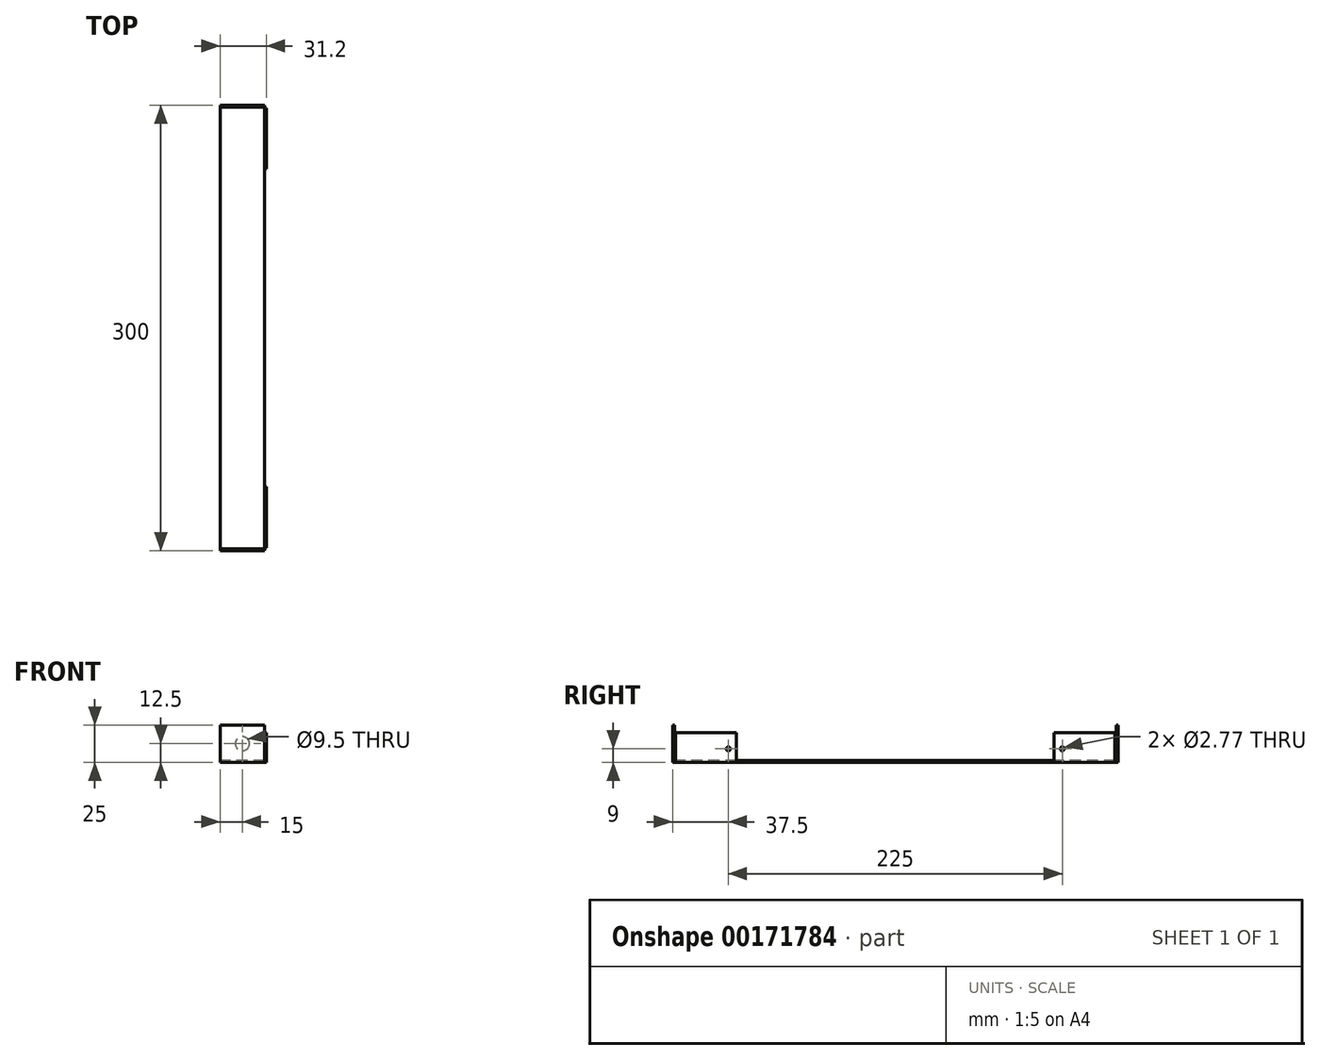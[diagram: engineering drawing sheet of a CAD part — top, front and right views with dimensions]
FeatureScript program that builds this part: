
annotation { "Feature Type Name" : "Feature", "Feature Type Description" : "" }
export const myFeature = defineFeature(function(context is Context, id is Id, definition is map)
    precondition{}
    {
        {
            var Q0;
            Q0=qCreatedBy(makeId("Right.planeOp"),FACE);
            var sketch = newSketch(context, id + "F0", { "sketchPlane" : qUnion([Q0])});
            skLineSegment(sketch, "E0.bottom", {"start": v(-150, 12.5) * mm, "end": v(-148.8, 12.5) * mm});
            skLineSegment(sketch, "E0.left", {"start": v(-150, 12.5) * mm, "end": v(-150, -12.5) * mm});
            skLineSegment(sketch, "E0.right", {"start": v(150, 12.5) * mm, "end": v(150, -12.5) * mm});
            skPoint(sketch, "E0.middle", {"position": v(0, 0) * mm});
            skLineSegment(sketch, "E1", {"start": v(-148.8, 12.5) * mm, "end": v(-148.79, -11.29) * mm});
            skLineSegment(sketch, "E2", {"start": v(-148.79, -11.29) * mm, "end": v(0, -11.29) * mm});
            skLineSegment(sketch, "E3.MirrorCS", {"start": v(148.79, -11.3) * mm, "end": v(0, -11.29) * mm});
            skLineSegment(sketch, "E4.MirrorCS", {"start": v(148.8, 12.5) * mm, "end": v(148.79, -11.29) * mm});
            skLineSegment(sketch, "E5.trimOffspring", {"start": v(148.8, 12.5) * mm, "end": v(150, 12.5) * mm});
            skPoint(sketch, "E6.end.orphan", {"position": v(0, -15) * mm});
            skLineSegment(sketch, "E7", {"start": v(-150, -12.5) * mm, "end": v(150, -12.5) * mm});
            skSolve(sketch);
        }
        {
            var Q0;
            Q0=qSketchRegion(id+"F0",true);
            extrude(context, id + "F1", {"entities" : qUnion([Q0]), "endBound" : BoundingType.SYMMETRIC, "depth" : 30 * mm});
        }
        {
            var Q0;
            Q0=makeQuery(id+"F1.opExtrude","SWEPT_FACE",FACE,{"disambiguationData":[OSD([sQuery(id+"F0.wireOp",EDGE,"E0.right")])]});
            var sketch = newSketch(context, id + "F2", { "sketchPlane" : qUnion([Q0])});
            skCircle(sketch, "E8", {"center": v(0, 0) * mm, "radius": 4.75 * mm});
            skSolve(sketch);
        }
        {
            var Q0;
            Q0=makeQuery(id+"F1.opExtrude","CAP_FACE",FACE,{"disambiguationData":[OSD([sQuery(id+"F0.wireOp",EDGE,"E0.bottom"),sQuery(id+"F0.wireOp",EDGE,"E0.left"),sQuery(id+"F0.wireOp",EDGE,"E0.right"),sQuery(id+"F0.wireOp",EDGE,"E1"),sQuery(id+"F0.wireOp",EDGE,"E2"),sQuery(id+"F0.wireOp",EDGE,"E3.MirrorCS"),sQuery(id+"F0.wireOp",EDGE,"E4.MirrorCS"),sQuery(id+"F0.wireOp",EDGE,"E5.trimOffspring"),sQuery(id+"F0.wireOp",EDGE,"E7")])],"isStart":false});
            var sketch = newSketch(context, id + "F3", { "sketchPlane" : qUnion([Q0])});
            skLineSegment(sketch, "E9.bottom", {"start": v(-148, -12.5) * mm, "end": v(-107, -12.5) * mm});
            skLineSegment(sketch, "E9.top", {"start": v(-148, 7.5) * mm, "end": v(-107, 7.5) * mm});
            skLineSegment(sketch, "E9.left", {"start": v(-148, -12.5) * mm, "end": v(-148, 7.5) * mm});
            skLineSegment(sketch, "E10.0", {"start": v(-107, -12.5) * mm, "end": v(-107, 7.5) * mm});
            skPoint(sketch, "E11.orphan", {"position": v(-71, 7.5) * mm});
            skPoint(sketch, "E12.orphan", {"position": v(-71, -12.5) * mm});
            skPoint(sketch, "E13.MirrorCS.end.orphan", {"position": v(71, 7.5) * mm});
            skPoint(sketch, "E13.MirrorCS.start.orphan", {"position": v(71, -12.5) * mm});
            skLineSegment(sketch, "E14.MirrorCS", {"start": v(107, -12.5) * mm, "end": v(107, 7.5) * mm});
            skLineSegment(sketch, "E15.MirrorCS", {"start": v(148, 7.5) * mm, "end": v(107, 7.5) * mm});
            skLineSegment(sketch, "E16.MirrorCS", {"start": v(148, -12.5) * mm, "end": v(148, 7.5) * mm});
            skLineSegment(sketch, "E17.MirrorCS", {"start": v(148, -12.5) * mm, "end": v(107, -12.5) * mm});
            skSolve(sketch);
        }
        {
            var Q0;
            Q0=qSketchRegion(id+"F3",true);
            extrude(context, id + "F4", {"entities" : qUnion([Q0]), "operationType" : NewBodyOperationType.ADD, "depth" : 1.2 * mm});
        }
        {
            var Q0;
            Q0=qSketchRegion(id+"F2",true);
            extrude(context, id + "F5", {"entities" : qUnion([Q0]), "operationType" : NewBodyOperationType.REMOVE, "endBound" : BoundingType.UP_TO_NEXT, "oppositeDirection" : true, "depth" : 25 * mm});
        }
        {
            var Q0;
            Q0=makeQuery(id+"F4.opExtrude","CAP_FACE",FACE,{"disambiguationData":[OSD([sQuery(id+"F3.wireOp",EDGE,"E9.bottom"),sQuery(id+"F3.wireOp",EDGE,"E9.top"),sQuery(id+"F3.wireOp",EDGE,"E9.left"),sQuery(id+"F3.wireOp",EDGE,"E9.right")])],"isStart":false});
            var sketch = newSketch(context, id + "F6", { "sketchPlane" : qUnion([Q0])});
            skCircle(sketch, "E18", {"center": v(-112.5, -3.5) * mm, "radius": 1.39 * mm});
            skCircle(sketch, "E19.MirrorC", {"center": v(112.5, -3.5) * mm, "radius": 1.39 * mm});
            skSolve(sketch);
        }
        {
            var Q0;
            Q0=qSketchRegion(id+"F6",true);
            extrude(context, id + "F7", {"entities" : qUnion([Q0]), "operationType" : NewBodyOperationType.REMOVE, "endBound" : BoundingType.UP_TO_NEXT, "oppositeDirection" : true, "depth" : 25 * mm});
        }
    });
